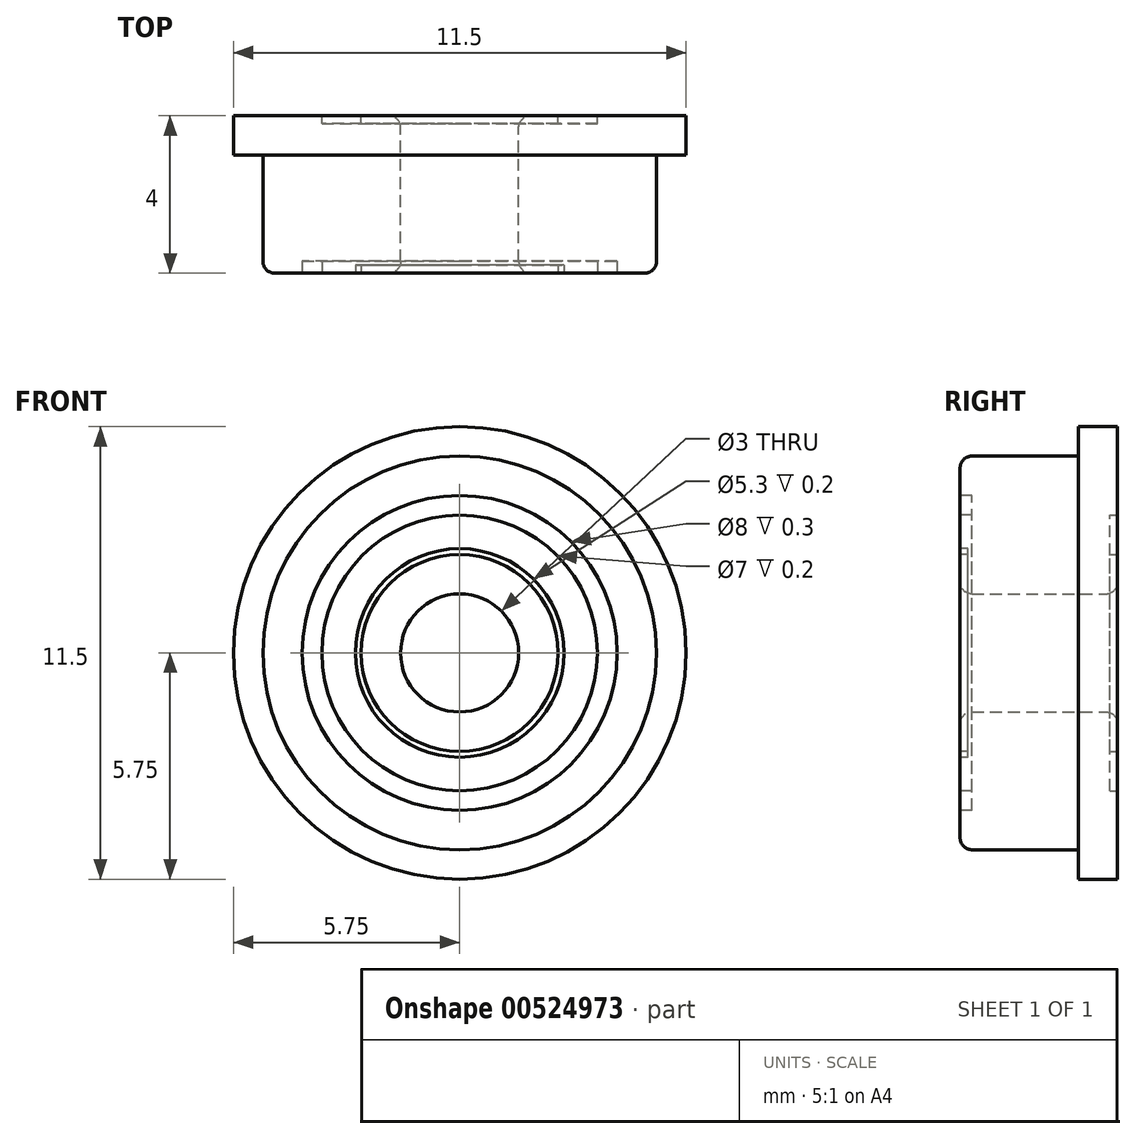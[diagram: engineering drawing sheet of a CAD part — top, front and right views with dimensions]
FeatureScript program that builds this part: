
annotation { "Feature Type Name" : "Feature", "Feature Type Description" : "" }
export const myFeature = defineFeature(function(context is Context, id is Id, definition is map)
    precondition{}
    {
        {
            var Q0;
            Q0=qCreatedBy(makeId("Front.planeOp"),FACE);
            var sketch = newSketch(context, id + "F0", { "sketchPlane" : qUnion([Q0])});
            skCircle(sketch, "E0", {"center": v(0, 0) * mm, "radius": 5.75 * mm});
            skCircle(sketch, "E1", {"center": v(0, 0) * mm, "radius": 1.5 * mm});
            skCircle(sketch, "E2", {"center": v(0, 0) * mm, "radius": 2.5 * mm});
            skCircle(sketch, "E3", {"center": v(0, 0) * mm, "radius": 3.5 * mm});
            skCircle(sketch, "E4", {"center": v(0, 0) * mm, "radius": 5 * mm});
            skSolve(sketch);
        }
        {
            var Q0;
            Q0=makeQuery(id+"F0.imprint","IMPRINT",FACE,{"disambiguationData":[TD([[makeQuery(id+"F0.imprint","IMPRINT",EDGE,{"derivedFrom":sQuery(id+"F0.wireOp",EDGE,"E0")}),1.0]])]});
            extrude(context, id + "F1", {"entities" : qUnion([Q0]), "depth" : 1 * mm, "offsetDistance" : 25 * mm});
        }
        {
            var Q0;
            Q0=makeQuery(id+"F0.imprint","IMPRINT",FACE,{"disambiguationData":[TD([[makeQuery(id+"F0.imprint","IMPRINT",EDGE,{"derivedFrom":sQuery(id+"F0.wireOp",EDGE,"E3")}),-1.0]])]});
            var Q1;
            Q1=makeQuery(id+"F0.imprint","IMPRINT",FACE,{"disambiguationData":[TD([[makeQuery(id+"F0.imprint","IMPRINT",EDGE,{"derivedFrom":sQuery(id+"F0.wireOp",EDGE,"E2")}),-1.0]])]});
            var Q2;
            Q2=makeQuery(id+"F0.imprint","IMPRINT",FACE,{"disambiguationData":[TD([[makeQuery(id+"F0.imprint","IMPRINT",EDGE,{"derivedFrom":sQuery(id+"F0.wireOp",EDGE,"E1")}),-1.0]])]});
            extrude(context, id + "F2", {"entities" : qUnion([Q0, Q1, Q2]), "operationType" : NewBodyOperationType.ADD, "depth" : 4 * mm, "offsetDistance" : 25 * mm});
        }
        {
            var Q0;
            Q0=makeQuery(id+"F2.opExtrude","CAP_EDGE",EDGE,{"disambiguationData":[OSD([sQuery(id+"F0.wireOp",EDGE,"E4")])],"isStart":false});
            var Q1;
            Q1=makeQuery(id+"F2.opExtrude","CAP_EDGE",EDGE,{"disambiguationData":[OSD([sQuery(id+"F0.wireOp",EDGE,"E1")])],"isStart":false});
            var Q2;
            Q2=makeQuery(id+"F2.opExtrude","CAP_EDGE",EDGE,{"disambiguationData":[OSD([sQuery(id+"F0.wireOp",EDGE,"E1")])],"isStart":true});
            fillet(context, id + "F3", {"entities" : qUnion([Q0, Q1, Q2]), "radius" : 0.3 * mm, "tangentPropagation" : true, "allowEdgeOverflow" : false});
        }
        {
            var Q0;
            Q0=makeQuery(id+"F2.opExtrude","CAP_FACE",FACE,{"disambiguationData":[OSD([sQuery(id+"F0.wireOp",EDGE,"E1"),sQuery(id+"F0.wireOp",EDGE,"E4")])],"isStart":false});
            var sketch = newSketch(context, id + "F4", { "sketchPlane" : qUnion([Q0])});
            skCircle(sketch, "E5", {"center": v(0, 0) * mm, "radius": 4 * mm});
            skCircle(sketch, "E6.0", {"center": v(0, 0) * mm, "radius": 2.5 * mm});
            skCircle(sketch, "E7", {"center": v(0, 0) * mm, "radius": 2.65 * mm});
            skCircle(sketch, "E8", {"center": v(0, 0) * mm, "radius": 3.5 * mm});
            skSolve(sketch);
        }
        {
            var Q0;
            Q0=makeQuery(id+"F4.imprint","IMPRINT",FACE,{"disambiguationData":[TD([[makeQuery(id+"F4.imprint","IMPRINT",EDGE,{"derivedFrom":sQuery(id+"F4.wireOp",EDGE,"E6.0")}),-1.0]])]});
            extrude(context, id + "F5", {"entities" : qUnion([Q0]), "operationType" : NewBodyOperationType.REMOVE, "oppositeDirection" : true, "depth" : 0.2 * mm, "offsetDistance" : 25 * mm});
        }
        {
            var Q0;
            Q0=makeQuery(id+"F4.imprint","IMPRINT",FACE,{"disambiguationData":[TD([[makeQuery(id+"F4.imprint","IMPRINT",EDGE,{"derivedFrom":sQuery(id+"F4.wireOp",EDGE,"E5")}),1.0]])]});
            extrude(context, id + "F6", {"entities" : qUnion([Q0]), "operationType" : NewBodyOperationType.REMOVE, "oppositeDirection" : true, "depth" : 0.3 * mm, "offsetDistance" : 25 * mm});
        }
        {
            var Q0;
            Q0=makeQuery(id+"F0.imprint","IMPRINT",FACE,{"disambiguationData":[TD([[makeQuery(id+"F0.imprint","IMPRINT",EDGE,{"derivedFrom":sQuery(id+"F0.wireOp",EDGE,"E2")}),-1.0]])]});
            extrude(context, id + "F7", {"entities" : qUnion([Q0]), "operationType" : NewBodyOperationType.REMOVE, "depth" : 0.2 * mm, "offsetDistance" : 25 * mm});
        }
    });
